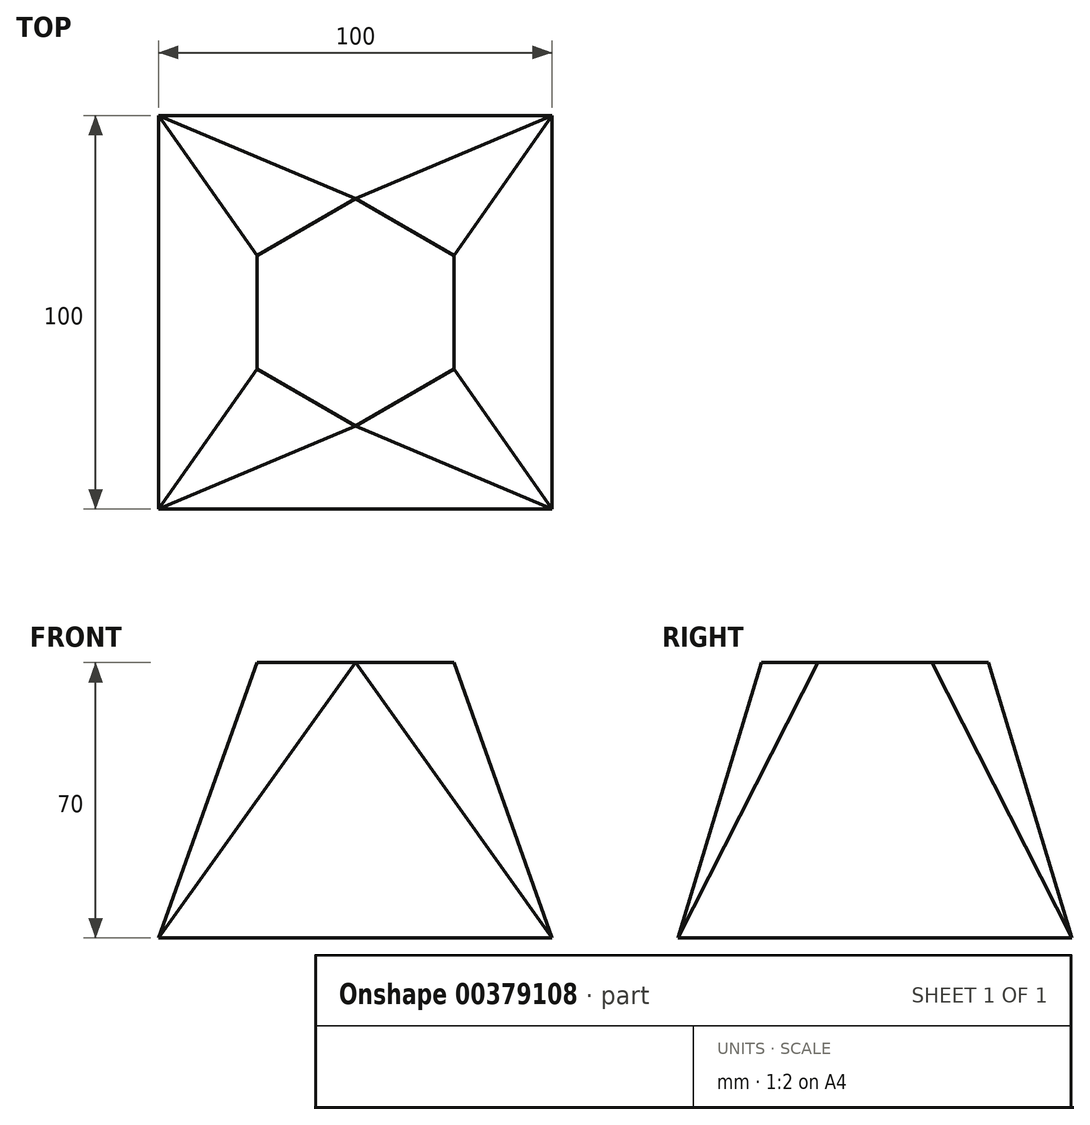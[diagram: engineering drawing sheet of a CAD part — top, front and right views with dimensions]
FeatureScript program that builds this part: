
annotation { "Feature Type Name" : "Feature", "Feature Type Description" : "" }
export const myFeature = defineFeature(function(context is Context, id is Id, definition is map)
    precondition{}
    {
        {
            var Q0;
            Q0=qCreatedBy(makeId("Top.planeOp"),FACE);
            var sketch = newSketch(context, id + "F0", { "sketchPlane" : qUnion([Q0])});
            skLineSegment(sketch, "E0.bottom", {"start": v(-50, 50) * mm, "end": v(50, 50) * mm});
            skLineSegment(sketch, "E0.top", {"start": v(-50, -50) * mm, "end": v(50, -50) * mm});
            skLineSegment(sketch, "E0.left", {"start": v(-50, 50) * mm, "end": v(-50, -50) * mm});
            skLineSegment(sketch, "E0.right", {"start": v(50, 50) * mm, "end": v(50, -50) * mm});
            skPoint(sketch, "E0.middle", {"position": v(0, 0) * mm});
            skSolve(sketch);
        }
        {
            var Q0;
            Q0=makeQuery(id+"F0.imprint","IMPRINT",FACE,{"disambiguationData":[TD([[makeQuery(id+"F0.imprint","IMPRINT",EDGE,{"derivedFrom":sQuery(id+"F0.wireOp",EDGE,"E0.bottom")}),-1.0]])]});
            cPlane(context, id + "F1", {"entities" : qUnion([Q0]), "cplaneType" : CPlaneType.OFFSET, "offset" : 70 * mm, "width" : 150 * mm, "height" : 150 * mm});
        }
        {
            var Q0;
            Q0=qCreatedBy(id+"F1.planeOp",FACE);
            var sketch = newSketch(context, id + "F2", { "sketchPlane" : qUnion([Q0])});
            skCircle(sketch, "E1.cCircle", {"center": v(0, 0) * mm, "radius": 25 * mm, "construction": true});
            skLineSegment(sketch, "E1.0", {"start": v(25, 14.43) * mm, "end": v(25, -14.43) * mm, "construction": true});
            skLineSegment(sketch, "E1.1", {"start": v(25, -14.43) * mm, "end": v(0, -28.87) * mm, "construction": true});
            skLineSegment(sketch, "E1.2", {"start": v(0, -28.87) * mm, "end": v(-25, -14.43) * mm, "construction": true});
            skLineSegment(sketch, "E1.3", {"start": v(-25, -14.43) * mm, "end": v(-25, 14.43) * mm, "construction": true});
            skLineSegment(sketch, "E1.4", {"start": v(-25, 14.43) * mm, "end": v(0, 28.87) * mm, "construction": true});
            skLineSegment(sketch, "E1.5", {"start": v(0, 28.87) * mm, "end": v(25, 14.43) * mm, "construction": true});
            skPoint(sketch, "E1.0.midPoint", {"position": v(25, 0) * mm});
            skLineSegment(sketch, "E2.bottom", {"start": v(-25, 28.87) * mm, "end": v(25, 28.87) * mm});
            skLineSegment(sketch, "E2.top", {"start": v(-25, -28.87) * mm, "end": v(25, -28.87) * mm});
            skLineSegment(sketch, "E2.left", {"start": v(-25, 28.87) * mm, "end": v(-25, -28.87) * mm});
            skLineSegment(sketch, "E2.right", {"start": v(25, 28.87) * mm, "end": v(25, -28.87) * mm});
            skSolve(sketch);
        }
        {
            var Q0;
            Q0=makeQuery(id+"F2.imprint","IMPRINT",FACE,{"disambiguationData":[TD([[makeQuery(id+"F2.imprint","IMPRINT",EDGE,{"derivedFrom":sQuery(id+"F2.wireOp",EDGE,"E2.bottom")}),-1.0]])]});
            var Q1;
            Q1=makeQuery(id+"F0.imprint","IMPRINT",FACE,{"disambiguationData":[TD([[makeQuery(id+"F0.imprint","IMPRINT",EDGE,{"derivedFrom":sQuery(id+"F0.wireOp",EDGE,"E0.bottom")}),-1.0]])]});
            loft(context, id + "F3", {"sheetProfilesArray" : [{ "sheetProfileEntities" : qUnion([Q0]) }, { "sheetProfileEntities" : qUnion([Q1]) }]});
        }
        {
            var Q0;
            Q0=qCreatedBy(id+"F1.planeOp",FACE);
            var sketch = newSketch(context, id + "F4", { "sketchPlane" : qUnion([Q0])});
            skCircle(sketch, "E3.cCircle", {"center": v(0, 0) * mm, "radius": 25 * mm, "construction": true});
            skLineSegment(sketch, "E3.0", {"start": v(-25, -14.43) * mm, "end": v(-25, 14.43) * mm});
            skLineSegment(sketch, "E3.1", {"start": v(-25, 14.43) * mm, "end": v(0, 28.87) * mm});
            skLineSegment(sketch, "E3.2", {"start": v(0, 28.87) * mm, "end": v(25, 14.43) * mm});
            skLineSegment(sketch, "E3.3", {"start": v(25, 14.43) * mm, "end": v(25, -14.43) * mm});
            skLineSegment(sketch, "E3.4", {"start": v(25, -14.43) * mm, "end": v(0, -28.87) * mm});
            skLineSegment(sketch, "E3.5", {"start": v(0, -28.87) * mm, "end": v(-25, -14.43) * mm});
            skPoint(sketch, "E3.0.midPoint", {"position": v(-25, 0) * mm});
            skLineSegment(sketch, "E4.bottom", {"start": v(-25, 28.87) * mm, "end": v(25, 28.87) * mm});
            skLineSegment(sketch, "E4.top", {"start": v(-25, -28.87) * mm, "end": v(25, -28.87) * mm});
            skLineSegment(sketch, "E4.left", {"start": v(-25, 28.87) * mm, "end": v(-25, -28.87) * mm});
            skLineSegment(sketch, "E4.right", {"start": v(25, 28.87) * mm, "end": v(25, -28.87) * mm});
            skSolve(sketch);
        }
        {
            var Q1;
            {var subQ0=sQuery(id+"F4.wireOp",EDGE,"E3.1");Q1=makeQuery(id+"F4.imprint","IMPRINT",FACE,{"disambiguationData":[TD([[makeQuery(id+"F4.imprint","IMPRINT",EDGE,{"derivedFrom":subQ0}),1.0]])]});}
            var Q2;
            Q2=makeQuery(id+"F3.opLoft","MID_CAP_VERTEX",VERTEX,{"disambiguationData":[OSD([sQuery(id+"F0.wireOp",EDGE,"E0.bottom"),sQuery(id+"F0.wireOp",EDGE,"E0.left")])],"capPos":1.0});
            loft(context, id + "F5", {"sheetProfilesArray" : [{ "sheetProfileEntities" : qUnion([Q1]) }, { "sheetProfileEntities" : qUnion([Q2]) }]});
        }
        {
            var Q0;
            {var subQ0=sQuery(id+"F4.wireOp",EDGE,"E3.1");Q0=makeQuery(id+"F5.opLoft","SWEPT_BODY",BODY,{"disambiguationData":[OSD([sQuery(id+"F0.wireOp",EDGE,"E0.bottom"),sQuery(id+"F0.wireOp",EDGE,"E0.left"),makeQuery(id+"F4.imprint","IMPRINT",FACE,{"disambiguationData":[TD([[makeQuery(id+"F4.imprint","IMPRINT",EDGE,{"derivedFrom":subQ0}),1.0]])]})])]});}
            var Q1;
            Q1=qCreatedBy(makeId("Front.planeOp"),FACE);
            mirror(context, id + "F6", {"entities" : qUnion([Q0]), "mirrorPlane" : qUnion([Q1])});
        }
        {
            var Q0;
            {var subQ0=sQuery(id+"F4.wireOp",EDGE,"E3.1");Q0=makeQuery(id+"F5.opLoft","SWEPT_BODY",BODY,{"disambiguationData":[OSD([sQuery(id+"F0.wireOp",EDGE,"E0.bottom"),sQuery(id+"F0.wireOp",EDGE,"E0.left"),makeQuery(id+"F4.imprint","IMPRINT",FACE,{"disambiguationData":[TD([[makeQuery(id+"F4.imprint","IMPRINT",EDGE,{"derivedFrom":subQ0}),1.0]])]})])]});}
            var Q1;
            {var subQ0=sQuery(id+"F4.wireOp",EDGE,"E3.1");Q1=makeQuery(id+"F6.opPattern","COPY",BODY,{"derivedFrom":makeQuery(id+"F5.opLoft","SWEPT_BODY",BODY,{"disambiguationData":[OSD([sQuery(id+"F0.wireOp",EDGE,"E0.bottom"),sQuery(id+"F0.wireOp",EDGE,"E0.left"),makeQuery(id+"F4.imprint","IMPRINT",FACE,{"disambiguationData":[TD([[makeQuery(id+"F4.imprint","IMPRINT",EDGE,{"derivedFrom":subQ0}),1.0]])]})])]}),"instanceName":"1"});}
            var Q2;
            Q2=qCreatedBy(makeId("Right.planeOp"),FACE);
            mirror(context, id + "F7", {"entities" : qUnion([Q0, Q1]), "mirrorPlane" : qUnion([Q2])});
        }
        {
            var Q0;
            {var subQ0=sQuery(id+"F4.wireOp",EDGE,"E3.1");Q0=makeQuery(id+"F5.opLoft","SWEPT_BODY",BODY,{"disambiguationData":[OSD([sQuery(id+"F0.wireOp",EDGE,"E0.bottom"),sQuery(id+"F0.wireOp",EDGE,"E0.left"),makeQuery(id+"F4.imprint","IMPRINT",FACE,{"disambiguationData":[TD([[makeQuery(id+"F4.imprint","IMPRINT",EDGE,{"derivedFrom":subQ0}),1.0]])]})])]});}
            var Q1;
            {var subQ0=sQuery(id+"F4.wireOp",EDGE,"E3.1");Q1=makeQuery(id+"F7.opPattern","COPY",BODY,{"derivedFrom":makeQuery(id+"F5.opLoft","SWEPT_BODY",BODY,{"disambiguationData":[OSD([sQuery(id+"F0.wireOp",EDGE,"E0.bottom"),sQuery(id+"F0.wireOp",EDGE,"E0.left"),makeQuery(id+"F4.imprint","IMPRINT",FACE,{"disambiguationData":[TD([[makeQuery(id+"F4.imprint","IMPRINT",EDGE,{"derivedFrom":subQ0}),1.0]])]})])]}),"instanceName":"1"});}
            var Q2;
            {var subQ0=sQuery(id+"F4.wireOp",EDGE,"E3.1");Q2=makeQuery(id+"F7.opPattern","COPY",BODY,{"derivedFrom":makeQuery(id+"F6.opPattern","COPY",BODY,{"derivedFrom":makeQuery(id+"F5.opLoft","SWEPT_BODY",BODY,{"disambiguationData":[OSD([sQuery(id+"F0.wireOp",EDGE,"E0.bottom"),sQuery(id+"F0.wireOp",EDGE,"E0.left"),makeQuery(id+"F4.imprint","IMPRINT",FACE,{"disambiguationData":[TD([[makeQuery(id+"F4.imprint","IMPRINT",EDGE,{"derivedFrom":subQ0}),1.0]])]})])]}),"instanceName":"1"}),"instanceName":"1"});}
            var Q3;
            {var subQ0=sQuery(id+"F4.wireOp",EDGE,"E3.1");Q3=makeQuery(id+"F6.opPattern","COPY",BODY,{"derivedFrom":makeQuery(id+"F5.opLoft","SWEPT_BODY",BODY,{"disambiguationData":[OSD([sQuery(id+"F0.wireOp",EDGE,"E0.bottom"),sQuery(id+"F0.wireOp",EDGE,"E0.left"),makeQuery(id+"F4.imprint","IMPRINT",FACE,{"disambiguationData":[TD([[makeQuery(id+"F4.imprint","IMPRINT",EDGE,{"derivedFrom":subQ0}),1.0]])]})])]}),"instanceName":"1"});}
            var Q4;
            Q4=makeQuery(id+"F3.opLoft","SWEPT_BODY",BODY,{"disambiguationData":[OSD([makeQuery(id+"F0.imprint","IMPRINT",FACE,{"disambiguationData":[TD([[makeQuery(id+"F0.imprint","IMPRINT",EDGE,{"derivedFrom":sQuery(id+"F0.wireOp",EDGE,"E0.bottom")}),-1.0]])]}),makeQuery(id+"F2.imprint","IMPRINT",FACE,{"disambiguationData":[TD([[makeQuery(id+"F2.imprint","IMPRINT",EDGE,{"derivedFrom":sQuery(id+"F2.wireOp",EDGE,"E2.bottom")}),-1.0]])]})])]});
            booleanBodies(context, id + "F8", {"operationType" : BooleanOperationType.SUBTRACTION, "tools" : qUnion([Q0, Q1, Q2, Q3]), "targets" : qUnion([Q4])});
        }
    });
